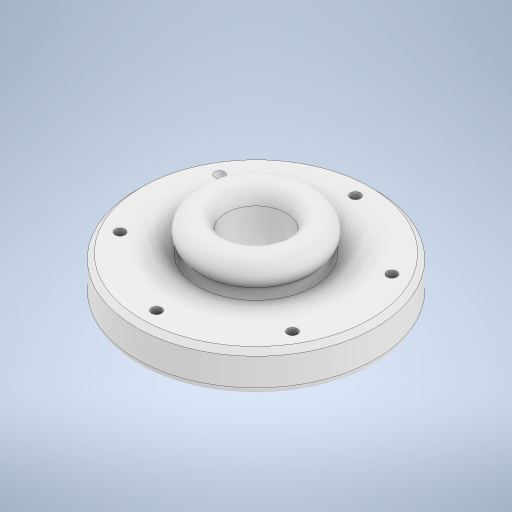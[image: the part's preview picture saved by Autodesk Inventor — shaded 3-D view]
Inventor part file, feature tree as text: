
AUTODESK INVENTOR PART (.ipt)
format: ipt  version: 2023 (Build 270158030, 158C)  size: 333,824 bytes
history: native  units: in
note: dims shown in document units (in); Inventor stores cm internally (conversion verified against a paired STEP export)
features: sketch x4, other x2, extrude x1, fillet x1, hole x1, pattern_circular x1, chamfer x1
ambient origin geometry x8: Origin, YZ Plane, XZ Plane, XY Plane, X Axis, Y Axis, Z Axis, Center Point
bodies: Solid1 (feature_tree)
feature tree (11):
  extrude  "Main-Body"  Depth=1.0in TaperAngle=0.0deg
  other  "Middle-Cutout"
  other  "Bump"
  fillet  "Fillet4"  Radius=1.0in
  hole  "Hole1"  [1 undecoded]
  pattern_circular  "Circular Pattern1"  [2 undecoded]
  chamfer  "Chamfer1"  Distance=2.5in
  sketch  "Sketch1"  dims[d0=6.0in d1=1.0in d2=0.0in d12=1.0in]
  sketch  "Sketch3"  dims[d13=360.0deg d17=360.0deg]
  sketch  "Sketch4"  dims[d19=0.75in]
  sketch  "Sketch6"  dims[d20=0.25in d22=6.1in d33=0.1875in d34=0.252in d35=0.75in d36=0.375in d37=0.25in d38=0.5635in d39=0.4173in d40=0.0in d41=2.5in d42=2.3622in d43=360.0deg d45=0.125in d46=0.125in d47=45.0deg d48=0.375in d50=0.5in d51=0.125in d52=1.5in]
note: 3 required parameter values undecoded (feature->parameter linkage not recoverable at this tier; creation-order binding heuristic only, values carry confidence <= 0.55)
